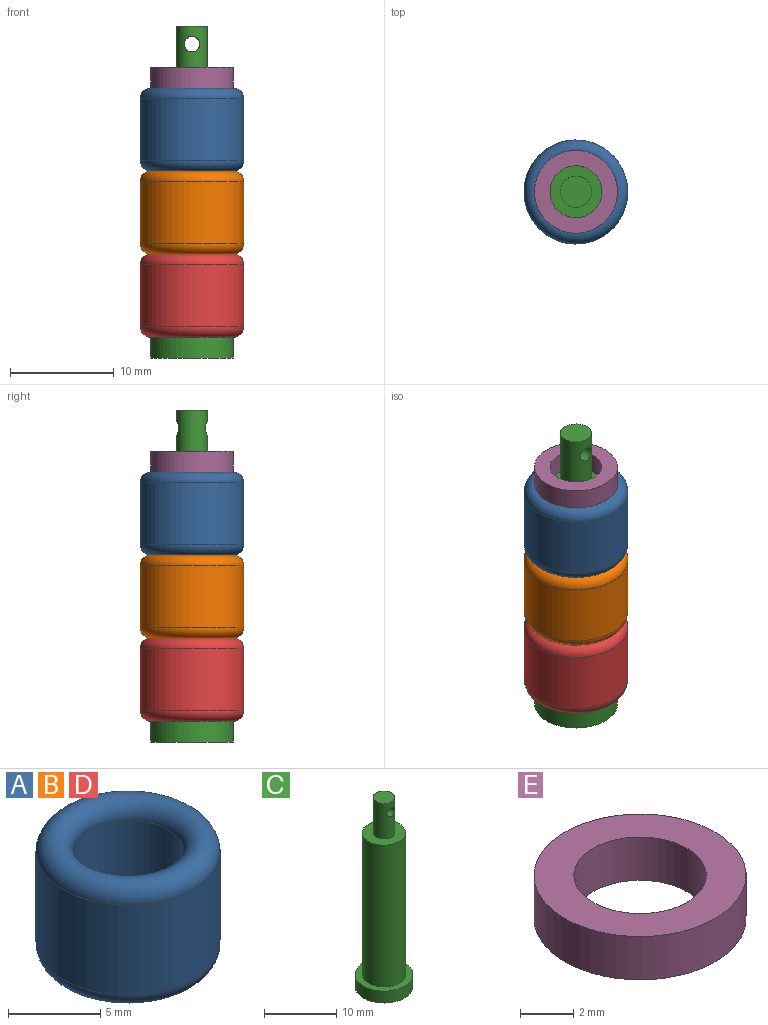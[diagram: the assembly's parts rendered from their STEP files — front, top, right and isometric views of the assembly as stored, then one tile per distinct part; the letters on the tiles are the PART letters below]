
ASSEMBLY  parts=5 mates=8
PART A: 4 faces, bbox 10.8x10.8x8 mm
  f0: cylinder r=3mm len=6mm, axis (0,0,-1), area 113.1mm2, adj f2,f3
  f1: cylinder r=5mm len=10mm, axis (0,0,-1), area 188.5mm2, adj f2,f3
  f2: torus R=4mm, axis (0,0,1), area 79mm2, adj f0,f1
  f3: torus R=4mm, axis (0,0,1), area 79mm2, adj f0,f1
PART B: same geometry as A
PART C: 8 faces, bbox 8x8x32 mm
  f0: cylinder r=4mm len=8mm, axis (0,0,-1), area 50.3mm2, adj f1,f2
  f1: plane 8x8mm, normal (0,0,1), area 22mm2, adj f0,f3
  f2: plane 8x8mm, normal (0,0,-1), area 50.3mm2, adj f0
  f3: cylinder r=3mm len=24mm, axis (0,0,-1), area 452.4mm2, adj f1,f4
  f4: plane 6x6mm, normal (0,0,1), area 21.2mm2, adj f3,f5
  f5: cylinder r=1.5mm len=6mm, axis (0,0,-1), area 52.9mm2, adj f4,f6,f7
  f6: plane 3x3mm, normal (0,0,1), area 7.1mm2, adj f5
  f7: cylinder r=0.75mm len=3mm, axis (0,-1,0), area 13.2mm2, adj f5
PART D: same geometry as A
PART E: 4 faces, bbox 8x8x2 mm
  f0: cylinder r=2.5mm len=5mm, axis (0,0,-1), area 31.4mm2, adj f2,f3
  f1: cylinder r=4mm len=8mm, axis (0,0,-1), area 50.3mm2, adj f2,f3
  f2: plane 8x8mm, normal (0,0,1), area 30.6mm2, adj f0,f1
  f3: plane 8x8mm, normal (0,0,-1), area 30.6mm2, adj f0,f1
PLACE A rot(axis=(0,0,1),0deg) t=(12.18,5.28,8.8)mm
PLACE B rot(axis=(0,0,1),0deg) t=(12.18,5.28,0.8)mm
PLACE C t=(12.18,5.28,-9.2)mm
PLACE D rot(axis=(0,0,1),0deg) t=(12.18,5.28,-7.2)mm
PLACE E t=(12.18,5.28,16.8)mm
MATE cylindrical C.f3 <-> D.f0  axis (0,0,-1) through (12.18,5.28,4.8)mm
MATE cylindrical A.f1 <-> C.f3  axis (0,0,-1) through (12.18,5.28,9.8)mm
MATE planar A.f1 <-> B.f1  axis (0,0,-1) through (12.18,5.28,12.8)mm
MATE planar D.f1 <-> C.f0  axis (0,0,1) through (12.18,5.28,-6.2)mm
MATE planar B.f1 <-> D.f1  axis (0,0,1) through (12.18,5.28,1.8)mm
MATE planar E.f1 <-> C.f3  axis (0,0,-1) through (12.18,5.28,16.8)mm
MATE cylindrical B.f1 <-> C.f3  axis (0,0,-1) through (12.18,5.28,1.8)mm
MATE cylindrical E.f0 <-> C.f0  axis (0,0,1) through (12.18,5.28,18.8)mm
